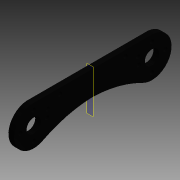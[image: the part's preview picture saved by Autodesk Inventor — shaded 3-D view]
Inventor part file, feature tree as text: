
AUTODESK INVENTOR PART (.ipt)
format: ipt  version: 2015 (Build 190159000, 159)  size: 112,128 bytes
history: native  units: mm
features: extrude x1, sketch x1
ambient origin geometry x8: Origin, YZ Plane, XZ Plane, XY Plane, X Axis, Y Axis, Z Axis, Center Point
bodies: Body1 (feature_tree)
feature tree (2):
  extrude  "Extrusion3"  Depth=3.5mm
  sketch  "Sketch1"  dims[d47=8.509mm d48=8.509mm d49=8.509mm d50=8.509mm d51=10.0mm d53=9.0mm d56=9.0mm d58=4.19811mm d61=75.0mm d62=3.5mm d63=0.0mm]
